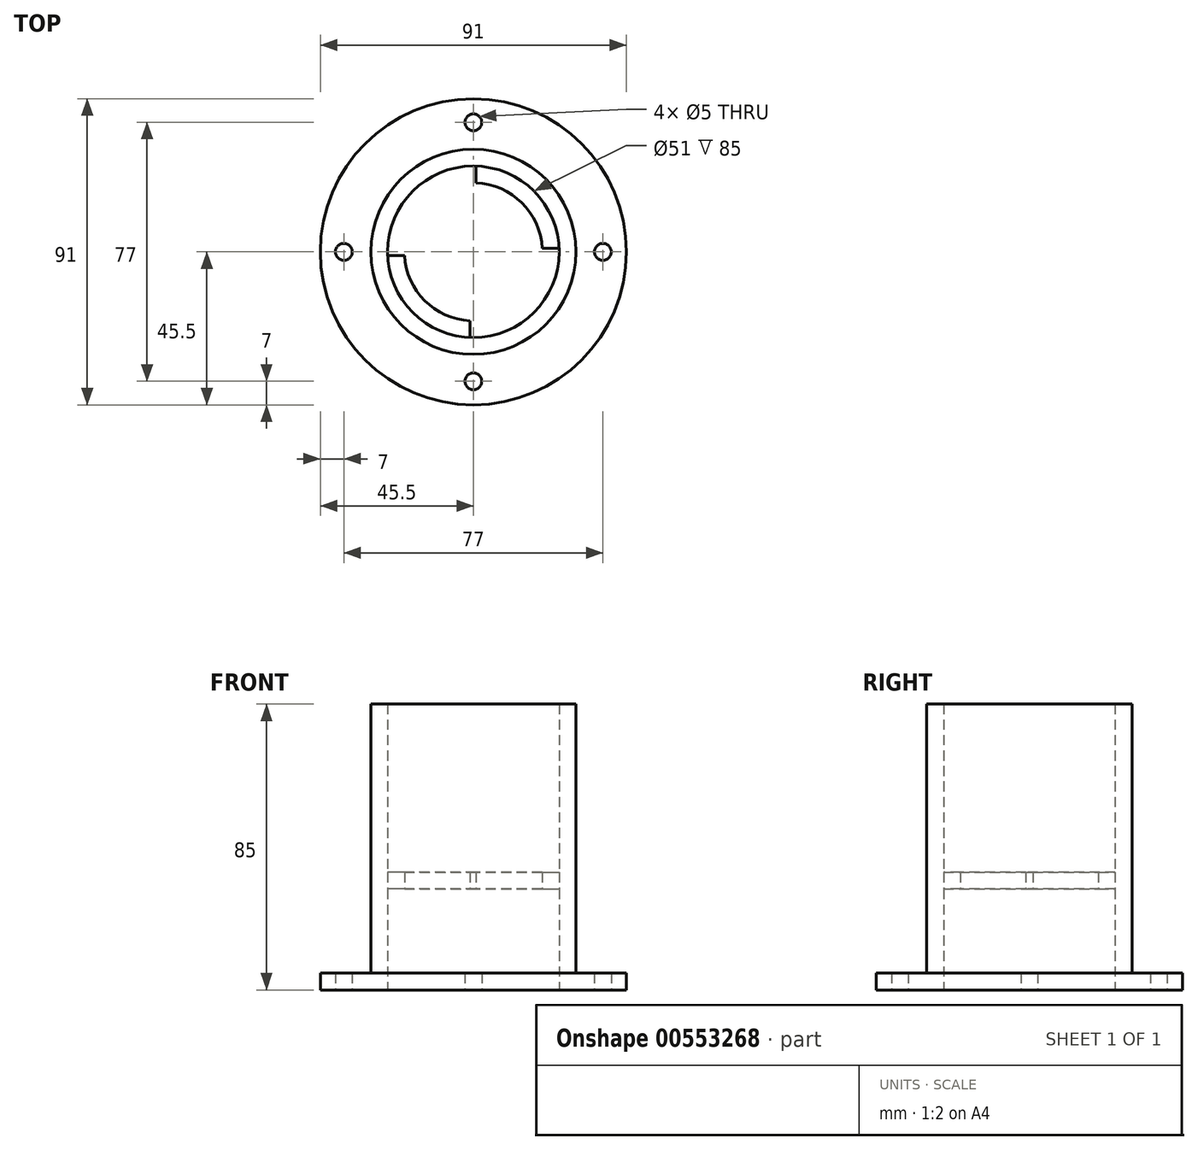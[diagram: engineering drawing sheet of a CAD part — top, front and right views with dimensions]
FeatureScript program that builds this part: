
annotation { "Feature Type Name" : "Feature", "Feature Type Description" : "" }
export const myFeature = defineFeature(function(context is Context, id is Id, definition is map)
    precondition{}
    {
        {
            var Q0;
            Q0=qCreatedBy(makeId("Top.planeOp"),FACE);
            var sketch = newSketch(context, id + "F0", { "sketchPlane" : qUnion([Q0])});
            skCircle(sketch, "E0", {"center": v(0, 0) * mm, "radius": 30.5 * mm});
            skCircle(sketch, "E1", {"center": v(0, 0) * mm, "radius": 45.5 * mm});
            skCircle(sketch, "E2", {"center": v(0, 0) * mm, "radius": 25.5 * mm});
            skPoint(sketch, "E3", {"position": v(-45.5, 0) * mm});
            skPoint(sketch, "E4", {"position": v(0, 45.5) * mm});
            skPoint(sketch, "E5", {"position": v(45.5, 0) * mm});
            skPoint(sketch, "E6", {"position": v(0, -45.5) * mm});
            skPoint(sketch, "E7", {"position": v(0, -38.5) * mm});
            skPoint(sketch, "E8", {"position": v(-38.5, 0) * mm});
            skPoint(sketch, "E9", {"position": v(0, 38.5) * mm});
            skPoint(sketch, "E10", {"position": v(38.5, 0) * mm});
            skArc(sketch, "E11", {"start": v(0.74, 20.49) * mm, "mid": v(14.4, 14.59) * mm, "end": v(20.48, 1) * mm});
            skLineSegment(sketch, "E12", {"start": v(0.74, 20.49) * mm, "end": v(0.74, 25.49) * mm});
            skLineSegment(sketch, "E13", {"start": v(20.48, 1) * mm, "end": v(25.48, 1) * mm});
            skArc(sketch, "E14", {"start": v(-0.95, -20.48) * mm, "mid": v(-14.46, -14.53) * mm, "end": v(-20.47, -1.05) * mm});
            skLineSegment(sketch, "E15", {"start": v(-20.47, -1.05) * mm, "end": v(-25.48, -1.05) * mm});
            skLineSegment(sketch, "E16", {"start": v(-0.95, -20.48) * mm, "end": v(-0.95, -25.48) * mm});
            skSolve(sketch);
        }
        {
            var Q0;
            Q0 = qSketchRegion(id + "F0", true);
            extrude(context, id + "F1", {"entities" : qUnion([Q0]), "depth" : 5 * mm, "offsetDistance" : 25 * mm});
        }
        {
            var Q0;
            Q0=makeQuery(id+"F0.imprint","IMPRINT",FACE,{"disambiguationData":[TD([[makeQuery(id+"F0.imprint","IMPRINT",EDGE,{"derivedFrom":sQuery(id+"F0.wireOp",EDGE,"E0")}),1.0]])]});
            extrude(context, id + "F2", {"entities" : qUnion([Q0]), "operationType" : NewBodyOperationType.ADD, "depth" : 85 * mm, "offsetDistance" : 25 * mm});
        }
        {
            var Q0;
            Q0=sQuery(id+"F0.wireOp",VERTEX,"E10");
            var Q1;
            Q1=sQuery(id+"F0.wireOp",VERTEX,"E8");
            var Q2;
            Q2=sQuery(id+"F0.wireOp",VERTEX,"E7");
            var Q3;
            Q3=sQuery(id+"F0.wireOp",VERTEX,"E9");
            var Q4;
            Q4=makeQuery(id+"F1.opExtrude","SWEPT_BODY",BODY,{"disambiguationData":[OSD([sQuery(id+"F0.wireOp",EDGE,"E0"),sQuery(id+"F0.wireOp",EDGE,"E1")])]});
            hole(context, id + "F3", {"style" : HoleStyle.SIMPLE, "endStyle" : HoleEndStyle.BLIND, "oppositeDirection" : true, "holeDiameter" : 5 * mm, "holeDepth" : 12 * mm, "isTappedThrough" : true, "tappedDepth" : 12 * mm, "tapClearance" : 3, "locations" : qUnion([Q0, Q1, Q2, Q3]), "scope" : qUnion([Q4])});
        }
        {
            var Q0;
            Q0=makeQuery(id+"F0.imprint","IMPRINT",FACE,{"disambiguationData":[TD([[makeQuery(id+"F0.imprint","IMPRINT",EDGE,{"derivedFrom":sQuery(id+"F0.wireOp",EDGE,"E11")}),1.0]])]});
            var Q1;
            Q1=makeQuery(id+"F0.imprint","IMPRINT",FACE,{"disambiguationData":[TD([[makeQuery(id+"F0.imprint","IMPRINT",EDGE,{"derivedFrom":sQuery(id+"F0.wireOp",EDGE,"E14")}),1.0]])]});
            extrude(context, id + "F4", {"entities" : qUnion([Q0, Q1]), "operationType" : NewBodyOperationType.ADD, "depth" : 35 * mm, "offsetDistance" : 25 * mm, "hasSecondDirection" : true, "secondDirectionOppositeDirection" : true, "secondDirectionDepth" : -30 * mm});
        }
    });
